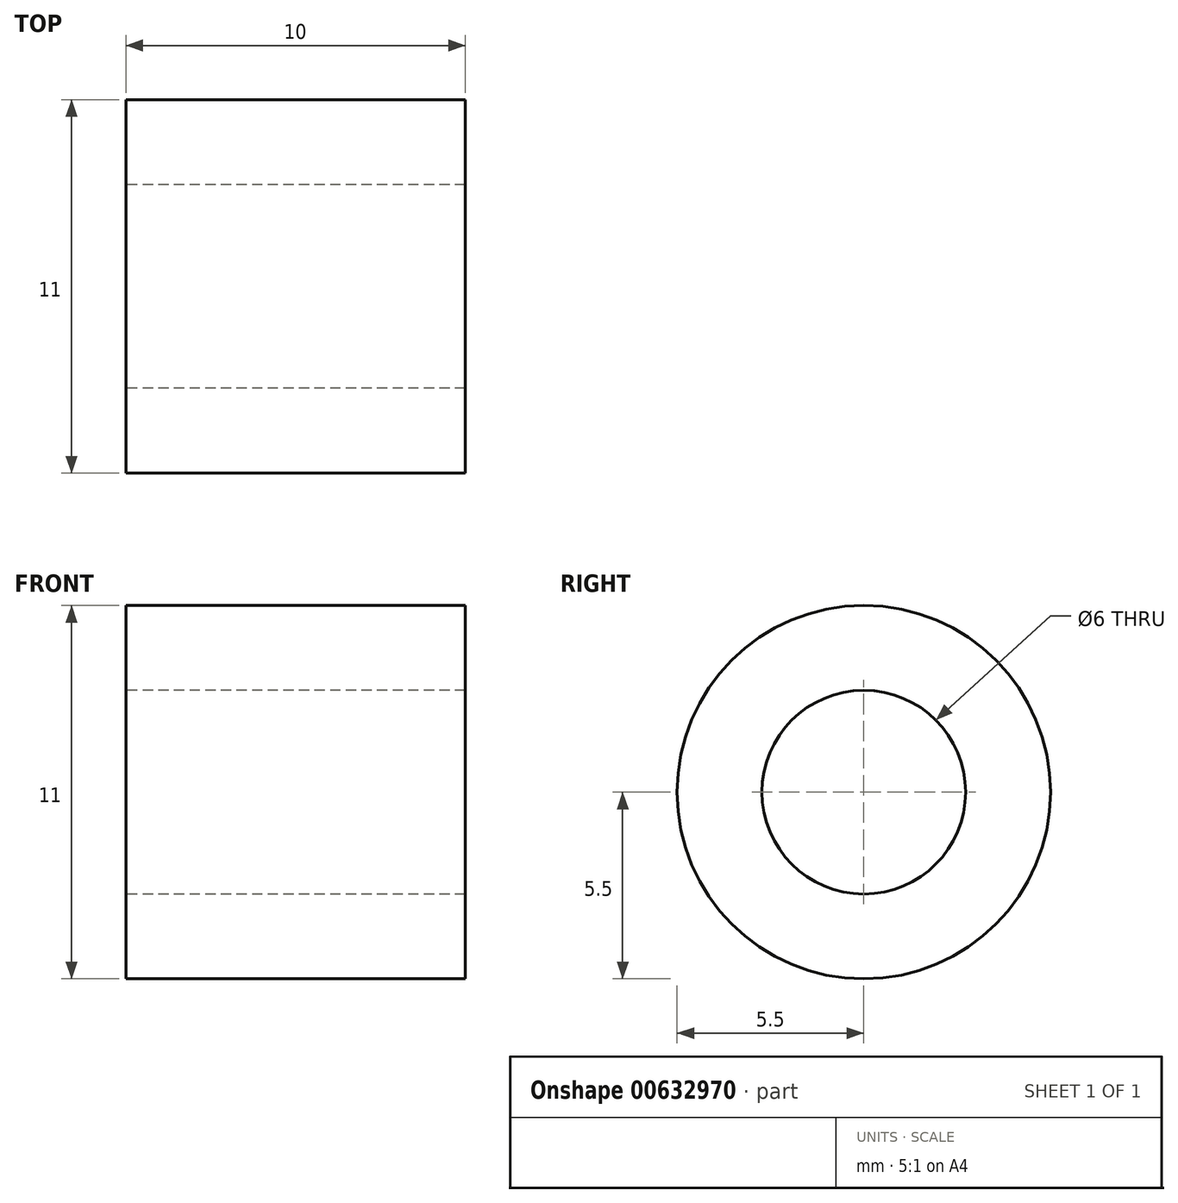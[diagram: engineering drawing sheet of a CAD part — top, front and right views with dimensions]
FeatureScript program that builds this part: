
annotation { "Feature Type Name" : "Feature", "Feature Type Description" : "" }
export const myFeature = defineFeature(function(context is Context, id is Id, definition is map)
    precondition{}
    {
        {
            var Q0;
            Q0=qCreatedBy(makeId("Right.planeOp"),FACE);
            var sketch = newSketch(context, id + "F0", { "sketchPlane" : qUnion([Q0])});
            skCircle(sketch, "E0", {"center": v(0, 0) * mm, "radius": 5.5 * mm});
            skCircle(sketch, "E1", {"center": v(0, 0) * mm, "radius": 3 * mm});
            skSolve(sketch);
        }
        {
            var Q0;
            Q0=makeQuery(id+"F0.imprint","IMPRINT",FACE,{"disambiguationData":[TD([[makeQuery(id+"F0.imprint","IMPRINT",EDGE,{"derivedFrom":sQuery(id+"F0.wireOp",EDGE,"E0")}),1.0]])]});
            extrude(context, id + "F1", {"entities" : qUnion([Q0]), "depth" : 10 * mm, "offsetDistance" : 25 * mm});
        }
    });
